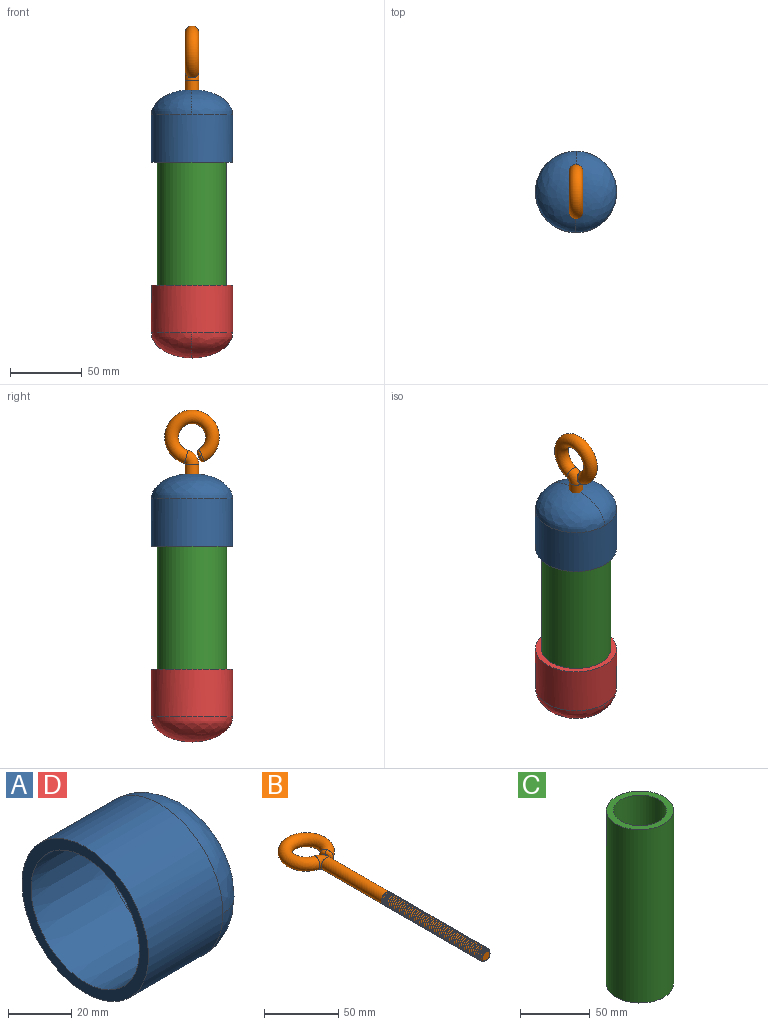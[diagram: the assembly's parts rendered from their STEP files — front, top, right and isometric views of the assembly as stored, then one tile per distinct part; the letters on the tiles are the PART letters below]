
ASSEMBLY  parts=4 mates=3
PART A: 7 faces, bbox 50.8x56.6x113.3 mm
  f0: bspline ~48.11x48.11mm, area 1304mm2, adj f2,f5
  f1: bspline ~56.64x56.64mm, area 1907.4mm2, adj f3,f4
  f2: cone r=25.4mm half-angle=0.4deg, axis (-1,0,0), area 5062.5mm2, adj f0,f5,f6
  f3: cylinder r=28.32mm len=56.64mm, axis (-1,0,0), area 5932.3mm2, adj f1,f4,f6
  f4: bspline ~56.64x56.64mm, area 1907.4mm2, adj f1,f3
  f5: bspline ~48.11x48.11mm, area 1304mm2, adj f0,f2
  f6: plane 56.64x56.64mm, normal (-1,0,0), area 667.4mm2, adj f2,f3
PART B: 72 faces, bbox 43.6x194.8x13.3 mm
  f0: torus R=5.56mm, axis (0,0,1), area 214mm2, adj f1,f4
  f1: torus R=14.29mm, axis (0,0,-1), area 2350.8mm2, adj f0,f2,f71
  f2: bspline ~9.52x5.19mm, area 41.6mm2, adj f1,f70,f71
  f3: cone r=25.4mm half-angle=45deg, axis (0,1,0), area 24.4mm2, adj f63,f64,f65,f66,f67,f68
  f4: cylinder r=4.76mm len=57.55mm, axis (0,1,0), area 1711.2mm2, adj f0,f5,f65,f67,f69
  f5: cylinder r=4.76mm len=9.53mm, axis (0,1,0), area 5.9mm2, adj f4,f6,f65,f67
  f6: cylinder r=4.76mm len=9.53mm, axis (0,1,0), area 5.9mm2, adj f5,f7,f65,f67
  f7: cylinder r=4.76mm len=9.53mm, axis (0,1,0), area 5.9mm2, adj f6,f8,f65,f67
  f8: cylinder r=4.76mm len=9.53mm, axis (0,1,0), area 5.9mm2, adj f7,f9,f65,f67
  f9: cylinder r=4.76mm len=9.53mm, axis (0,1,0), area 5.9mm2, adj f8,f10,f65,f67
  f10: cylinder r=4.76mm len=9.53mm, axis (0,1,0), area 5.9mm2, adj f9,f11,f65,f67
  f11: cylinder r=4.76mm len=9.53mm, axis (0,1,0), area 5.9mm2, adj f10,f12,f65,f67
  f12: cylinder r=4.76mm len=9.53mm, axis (0,1,0), area 5.9mm2, adj f11,f13,f65,f67
  f13: cylinder r=4.76mm len=9.53mm, axis (0,1,0), area 5.9mm2, adj f12,f14,f65,f67
  f14: cylinder r=4.76mm len=9.53mm, axis (0,1,0), area 5.9mm2, adj f13,f15,f65,f67
  f15: cylinder r=4.76mm len=9.53mm, axis (0,1,0), area 5.9mm2, adj f14,f16,f65,f67
  f16: cylinder r=4.76mm len=9.53mm, axis (0,1,0), area 5.9mm2, adj f15,f17,f65,f67
  f17: cylinder r=4.76mm len=9.53mm, axis (0,1,0), area 5.9mm2, adj f16,f18,f65,f67
  f18: cylinder r=4.76mm len=9.53mm, axis (0,1,0), area 5.9mm2, adj f17,f19,f65,f67
  f19: cylinder r=4.76mm len=9.53mm, axis (0,1,0), area 5.9mm2, adj f18,f20,f65,f67
  f20: cylinder r=4.76mm len=9.53mm, axis (0,1,0), area 5.9mm2, adj f19,f21,f65,f67
  f21: cylinder r=4.76mm len=9.53mm, axis (0,1,0), area 5.9mm2, adj f20,f22,f65,f67
  f22: cylinder r=4.76mm len=9.53mm, axis (0,1,0), area 5.9mm2, adj f21,f23,f65,f67
  f23: cylinder r=4.76mm len=9.53mm, axis (0,1,0), area 5.9mm2, adj f22,f24,f65,f67
  f24: cylinder r=4.76mm len=9.53mm, axis (0,1,0), area 5.9mm2, adj f23,f25,f65,f67
  f25: cylinder r=4.76mm len=9.53mm, axis (0,1,0), area 5.9mm2, adj f24,f26,f65,f67
  f26: cylinder r=4.76mm len=9.53mm, axis (0,1,0), area 5.9mm2, adj f25,f27,f65,f67
  f27: cylinder r=4.76mm len=9.53mm, axis (0,1,0), area 5.9mm2, adj f26,f28,f65,f67
  f28: cylinder r=4.76mm len=9.53mm, axis (0,1,0), area 5.9mm2, adj f27,f29,f65,f67
  f29: cylinder r=4.76mm len=9.53mm, axis (0,1,0), area 5.9mm2, adj f28,f30,f65,f67
  f30: cylinder r=4.76mm len=9.53mm, axis (0,1,0), area 5.9mm2, adj f29,f31,f65,f67
  f31: cylinder r=4.76mm len=9.53mm, axis (0,1,0), area 5.9mm2, adj f30,f32,f65,f67
  f32: cylinder r=4.76mm len=9.53mm, axis (0,1,0), area 5.9mm2, adj f31,f33,f65,f67
  f33: cylinder r=4.76mm len=9.53mm, axis (0,1,0), area 5.9mm2, adj f32,f34,f65,f67
  f34: cylinder r=4.76mm len=9.53mm, axis (0,1,0), area 5.9mm2, adj f33,f35,f65,f67
  f35: cylinder r=4.76mm len=9.53mm, axis (0,1,0), area 5.9mm2, adj f34,f36,f65,f67
  f36: cylinder r=4.76mm len=9.53mm, axis (0,1,0), area 5.9mm2, adj f35,f37,f65,f67
  f37: cylinder r=4.76mm len=9.53mm, axis (0,1,0), area 5.9mm2, adj f36,f38,f65,f67
  f38: cylinder r=4.76mm len=9.53mm, axis (0,1,0), area 5.9mm2, adj f37,f39,f65,f67
  f39: cylinder r=4.76mm len=9.53mm, axis (0,1,0), area 5.9mm2, adj f38,f40,f65,f67
  f40: cylinder r=4.76mm len=9.53mm, axis (0,1,0), area 5.9mm2, adj f39,f41,f65,f67
  f41: cylinder r=4.76mm len=9.53mm, axis (0,1,0), area 5.9mm2, adj f40,f42,f65,f67
  f42: cylinder r=4.76mm len=9.53mm, axis (0,1,0), area 5.9mm2, adj f41,f43,f65,f67
  f43: cylinder r=4.76mm len=9.53mm, axis (0,1,0), area 5.9mm2, adj f42,f44,f65,f67
  f44: cylinder r=4.76mm len=9.53mm, axis (0,1,0), area 5.9mm2, adj f43,f45,f65,f67
  f45: cylinder r=4.76mm len=9.53mm, axis (0,1,0), area 5.9mm2, adj f44,f46,f65,f67
  f46: cylinder r=4.76mm len=9.53mm, axis (0,1,0), area 5.9mm2, adj f45,f47,f65,f67
  f47: cylinder r=4.76mm len=9.53mm, axis (0,1,0), area 5.9mm2, adj f46,f48,f65,f67
  f48: cylinder r=4.76mm len=9.53mm, axis (0,1,0), area 5.9mm2, adj f47,f49,f65,f67
  f49: cylinder r=4.76mm len=9.53mm, axis (0,1,0), area 5.9mm2, adj f48,f50,f65,f67
  f50: cylinder r=4.76mm len=9.53mm, axis (0,1,0), area 5.9mm2, adj f49,f51,f65,f67
  f51: cylinder r=4.76mm len=9.53mm, axis (0,1,0), area 5.9mm2, adj f50,f52,f65,f67
  f52: cylinder r=4.76mm len=9.53mm, axis (0,1,0), area 5.9mm2, adj f51,f53,f65,f67
  f53: cylinder r=4.76mm len=9.53mm, axis (0,1,0), area 5.9mm2, adj f52,f54,f65,f67
  f54: cylinder r=4.76mm len=9.53mm, axis (0,1,0), area 5.9mm2, adj f53,f55,f65,f67
  f55: cylinder r=4.76mm len=9.53mm, axis (0,1,0), area 5.9mm2, adj f54,f56,f65,f67
  f56: cylinder r=4.76mm len=9.53mm, axis (0,1,0), area 5.9mm2, adj f55,f57,f65,f67
  f57: cylinder r=4.76mm len=9.53mm, axis (0,1,0), area 5.9mm2, adj f56,f58,f65,f67
  f58: cylinder r=4.76mm len=9.53mm, axis (0,1,0), area 5.9mm2, adj f57,f59,f65,f67
  f59: cylinder r=4.76mm len=9.53mm, axis (0,1,0), area 5.9mm2, adj f58,f60,f65,f67
  f60: cylinder r=4.76mm len=9.53mm, axis (0,1,0), area 5.9mm2, adj f59,f61,f65,f67
  f61: cylinder r=4.76mm len=9.53mm, axis (0,1,0), area 5.9mm2, adj f60,f62,f65,f67
  f62: cylinder r=4.76mm len=9.53mm, axis (0,1,0), area 5.9mm2, adj f61,f63,f65,f67
  f63: cylinder r=4.76mm len=9.53mm, axis (0,1,0), area 5.9mm2, adj f3,f62,f64,f65,f67
  f64: cylinder r=4.76mm len=3.23mm, axis (0,1,0), area 0.3mm2, adj f3,f63,f65
  f65: bspline ~96.27x11mm, area 1894.5mm2, adj f3,f4,f5,f6,f7,f8,f9,f10
  f66: cylinder r=3.73mm len=95.08mm, axis (0,1,0), area 168.2mm2, adj f3,f65,f67,f69
  f67: bspline ~95.67x9.38mm, area 1895mm2, adj f3,f4,f5,f6,f7,f8,f9,f10
  f68: plane 7.12x7.12mm, normal (0,-1,0), area 39.8mm2, adj f3
  f69: plane 11.85x11.85mm, normal (0,-1,0), area 14mm2, adj f4,f65,f66,f67
  f70: plane 4.77x4.57mm, normal (-0.94,-0.33,0), area 18.1mm2, adj f2,f71
  f71: bspline ~9.52x4.79mm, area 49.4mm2, adj f1,f2,f70
PART C: 4 faces, bbox 48.3x48.3x152.4 mm
  f0: cylinder r=19.05mm len=152.4mm, axis (0,0,1), area 18241.5mm2, adj f2,f3
  f1: cylinder r=24.13mm len=152.4mm, axis (0,0,1), area 23105.9mm2, adj f2,f3
  f2: plane 48.26x48.26mm, normal (0,0,1), area 689.1mm2, adj f0,f1
  f3: plane 48.26x48.26mm, normal (0,0,-1), area 689.1mm2, adj f0,f1
PART D: same geometry as A
PLACE A rot(axis=(0,-1,0),90deg) t=(58.6,60.38,-4.47)mm
PLACE B rot(axis=(0.58,-0.58,-0.58),120deg) t=(58.6,60.38,46.33)mm
PLACE C t=(58.6,60.38,-148.93)mm
PLACE D rot(axis=(0,1,0),90deg) t=(58.6,60.38,-140.99)mm
MATE fastened A.f2 <-> C.f0  axis (0,0,-1) through (58.6,60.38,3.47)mm
MATE fastened D.f2 <-> C.f0  axis (0,0,1) through (58.6,60.38,-148.93)mm
MATE slider B.f3 <-> A.f2  axis (0,0,1) through (58.6,60.38,46.33)mm
